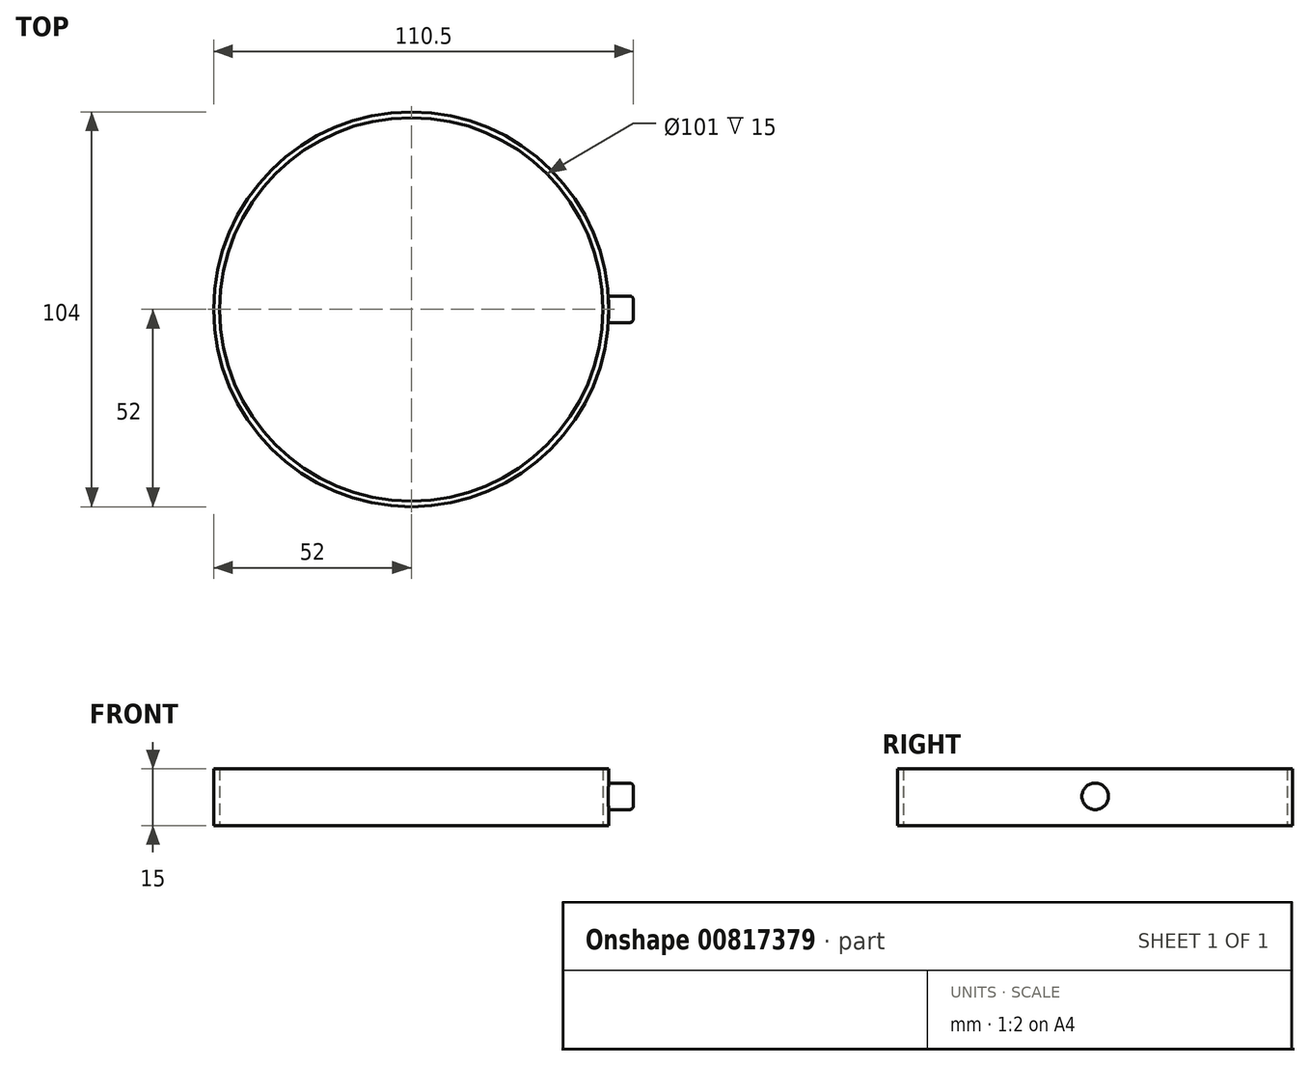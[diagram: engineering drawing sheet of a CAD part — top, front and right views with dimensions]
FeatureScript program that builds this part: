
annotation { "Feature Type Name" : "Feature", "Feature Type Description" : "" }
export const myFeature = defineFeature(function(context is Context, id is Id, definition is map)
    precondition{}
    {
        {
            var Q0;
            Q0=qCreatedBy(makeId("Top.planeOp"),FACE);
            var sketch = newSketch(context, id + "F0", { "sketchPlane" : qUnion([Q0])});
            skCircle(sketch, "E0", {"center": v(0, 0) * mm, "radius": 50.5 * mm});
            skCircle(sketch, "E1.0", {"center": v(0, 0) * mm, "radius": 52 * mm});
            skSolve(sketch);
        }
        {
            var Q0;
            Q0=makeQuery(id+"F0.imprint","IMPRINT",FACE,{"disambiguationData":[TD([[makeQuery(id+"F0.imprint","IMPRINT",EDGE,{"derivedFrom":sQuery(id+"F0.wireOp",EDGE,"E0")}),-1.0]])]});
            extrude(context, id + "F1", {"entities" : qUnion([Q0]), "depth" : 15 * mm, "offsetDistance" : 25 * mm});
        }
        {
            var Q0;
            Q0=qCreatedBy(makeId("Right.planeOp"),FACE);
            cPlane(context, id + "F2", {"entities" : qUnion([Q0]), "cplaneType" : CPlaneType.OFFSET, "offset" : 51.5 * mm, "width" : 150 * mm, "height" : 150 * mm});
        }
        {
            var Q0;
            Q0=qCreatedBy(id+"F2.planeOp",FACE);
            var sketch = newSketch(context, id + "F3", { "sketchPlane" : qUnion([Q0])});
            skCircle(sketch, "E2", {"center": v(0, 7.73) * mm, "radius": 3.5 * mm});
            skSolve(sketch);
        }
        {
            var Q0;
            Q0 = qSketchRegion(id + "F3", true);
            extrude(context, id + "F4", {"entities" : qUnion([Q0]), "operationType" : NewBodyOperationType.ADD, "depth" : 7 * mm, "offsetDistance" : 25 * mm});
        }
        {
            var Q0;
            Q0=makeQuery(id+"F4.opExtrude","CAP_EDGE",EDGE,{"disambiguationData":[OSD([sQuery(id+"F3.wireOp",EDGE,"E2")])],"isStart":false});
            fillet(context, id + "F5", {"entities" : qUnion([Q0]), "radius" : 1 * mm, "tangentPropagation" : true, "allowEdgeOverflow" : false});
        }
    });
